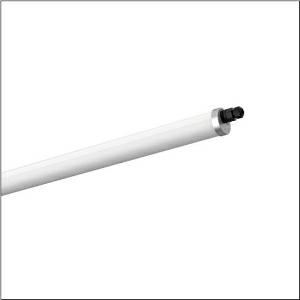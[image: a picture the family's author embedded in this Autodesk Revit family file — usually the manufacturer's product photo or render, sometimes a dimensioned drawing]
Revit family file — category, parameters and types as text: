
# Revit family: monsun_r__31_tube_51ft107n460a_2b58
name_source: partatom
category: Lighting Fixtures
units: mm (PartAtom-declared; Revit-internal decimal feet)

## family parameters
Cut with Voids When Loaded = No
Host = Face
Light Source = No
Part Type = Normal
Room Calculation Point = No
Round Connector Dimension = Use Diameter
Shared = No

## types (1)
- Monsun® 31 Tube (1 x LED, 6500 lm, 40 W, 4000K)
    Apparent Load = 40 VA
    CIE Flux Codes = 42 71 90 91 100
    Color Rendering = 80
    Color Temperature = 4000K
    Default Elevation = 1800 mm
    Description = Monsun® 31 Tube, tubular luminaire, primary optical cover: diffuser, of PMMA, light emission: direct distribution, primary light characteristic: symmetric, installation type: suspended mounting, surface-mounted, LED, rated luminous flux: 6.500lm, luminous efficacy: 160lm/W, light colour: 840, colour temperature: 4000K, control gear: ON/OFF, with with 1 terminal, 3-pole, max. 2.5mm², through-wiring: 3x 1.5mm², mains connection: 220..240V, AC, 50/60Hz, rated input power: 40W, housing, cylindrical, of PMMA, semi-transparent, matt white, with luminaire and ceiling fastening, V4A, mounting with brackets of stainless steel, length: 1.560mm, diameter: 75mm, end cap, of stainless steel (V4A), protection rating (complete): IP67/IP69K, insulation class (complete): insulation class I (protective earthing), certification: CE, UKCA, impact resistance: IK07, permissible operating ambient temperature: -20..+40°C, corresponds to IFS (International Featured Standards) requirements for safety and quality in the food industry, usage in unprotected outdoor areas possible with horizontal mounting, contact your sales advisor before using the luminaires in applications with unclear chemical exposure, large temperature fluctuations or condensation-forming humidity, packaging unit: 1 piece
    Height = 83 mm
    Lamp = 1 x LED
    Lamp Light Flux = 6500 lm
    Lamp Power = 40 W
    Lamp count = 1
    Length = 1560 mm
    Luminous efficacy = 163 lm/W
    Manufacturer = Siteco
    ModVariant = No
    Model = 51FT107N460A
    Mounting Place = Ceiling
    Mounting Type = Pendant
    Number of Poles = 1
    OnlyDefault = Yes
    Power Factor = 1
    Product Name = Monsun® 31 Tube
    Product group = tubular luminaire
    ProductGroupID = 907
    Protection Class = Protection class I
    RLX_Detail_Level = 1
    RLX_Emergency_Light_Flux = 0 lm
    RLX_Emergency_Type = 0
    RLX_Emergency_Type_DB = No
    RlxData = <blob elided: 25305 chars, md5=5ebcaaa6>
    Socket = socket
    Standby Power = 0 W
    System Light Flux = 6500 lm
    System Power = 40 W
    Type Comments = Product without accessories
    Type Image = l_1228461.jpg
    URL = http://relux.com
    VarID = ---
    Voltage = 0 V
    Weight = 0.00 kg
    Width = 75 mm

## geometry (parser evidence)
native form markers: Blend x4, Sweep x15
no freeform markers — native parametric forms only
